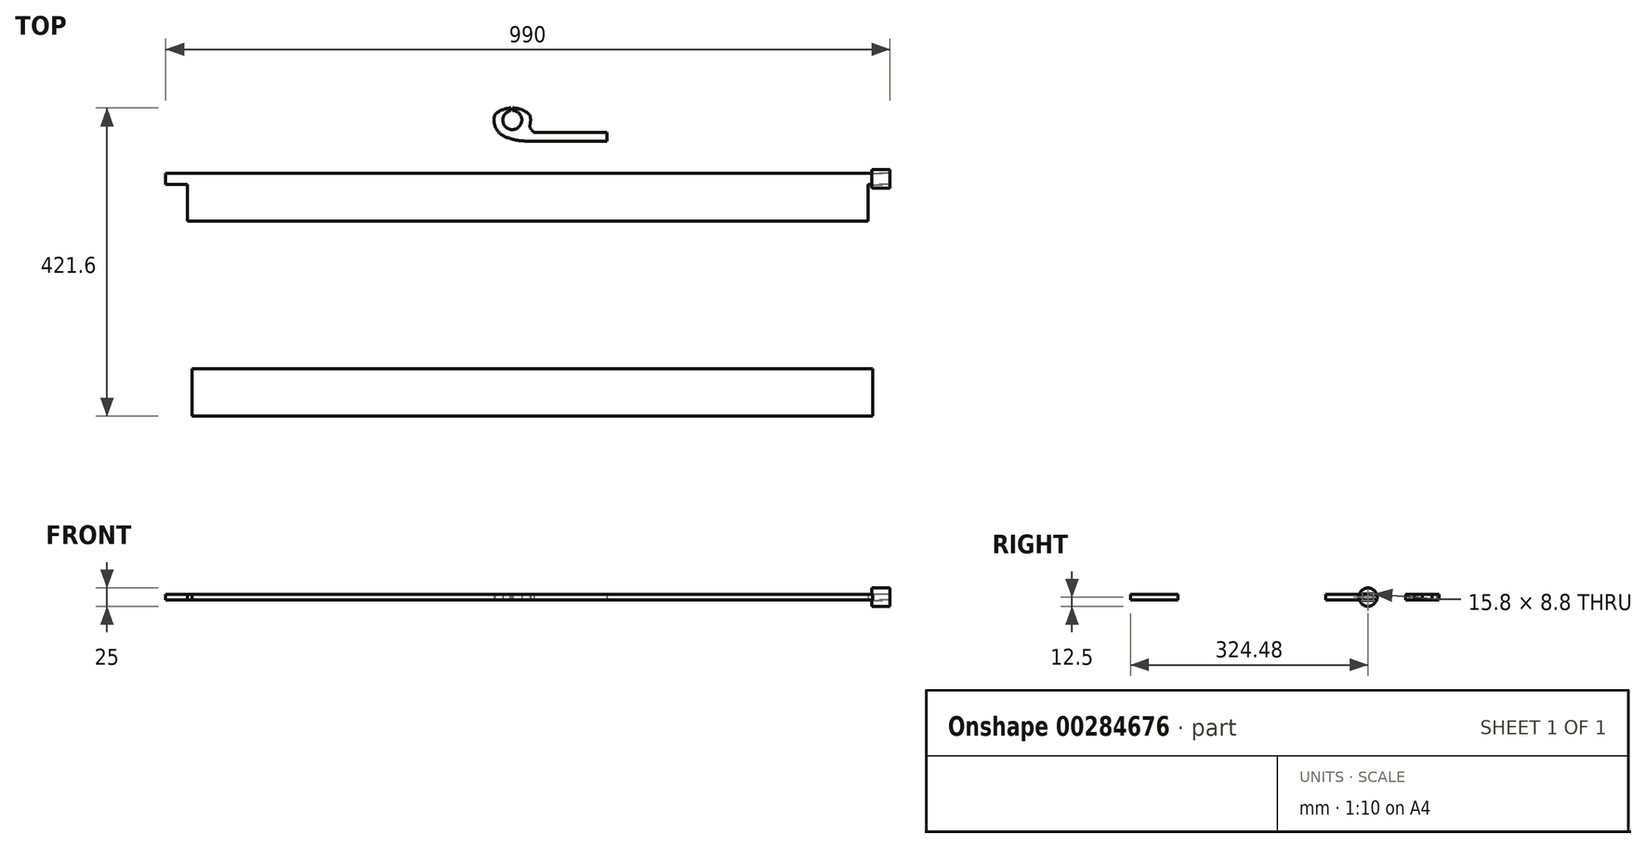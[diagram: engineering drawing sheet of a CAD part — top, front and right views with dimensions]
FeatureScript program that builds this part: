
annotation { "Feature Type Name" : "Feature", "Feature Type Description" : "" }
export const myFeature = defineFeature(function(context is Context, id is Id, definition is map)
    precondition{}
    {
        {
            var Q0;
            Q0=qCreatedBy(makeId("Top.planeOp"),FACE);
            var sketch = newSketch(context, id + "F0", { "sketchPlane" : qUnion([Q0])});
            skLineSegment(sketch, "E0.bottom", {"start": v(495, 7.5) * mm, "end": v(-495, 7.5) * mm});
            skLineSegment(sketch, "E0.top", {"start": v(495, -7.5) * mm, "end": v(465, -7.5) * mm});
            skLineSegment(sketch, "E0.left", {"start": v(495, 7.5) * mm, "end": v(495, -7.5) * mm});
            skLineSegment(sketch, "E0.right", {"start": v(-495, 7.5) * mm, "end": v(-495, -7.5) * mm});
            skPoint(sketch, "E0.middle", {"position": v(0, 0) * mm});
            skLineSegment(sketch, "E1", {"start": v(495, 0) * mm, "end": v(465, 0) * mm, "construction": true});
            skLineSegment(sketch, "E2.top", {"start": v(465, -57.5) * mm, "end": v(-465, -57.5) * mm});
            skLineSegment(sketch, "E2.left", {"start": v(465, -7.5) * mm, "end": v(465, -57.5) * mm});
            skLineSegment(sketch, "E2.right", {"start": v(-465, -7.5) * mm, "end": v(-465, -57.5) * mm});
            skLineSegment(sketch, "E3", {"start": v(-495, 0) * mm, "end": v(-465, 0) * mm, "construction": true});
            skLineSegment(sketch, "E4.trimOffspring", {"start": v(-465, -7.5) * mm, "end": v(-495, -7.5) * mm});
            skLineSegment(sketch, "E5.bottom", {"start": v(-465, -57.5) * mm, "end": v(-465, -57.5) * mm});
            skLineSegment(sketch, "E5.top", {"start": v(-465, 7.5) * mm, "end": v(-465, 7.5) * mm});
            skLineSegment(sketch, "E5.left", {"start": v(-465, -57.5) * mm, "end": v(-465, 7.5) * mm});
            skLineSegment(sketch, "E5.right", {"start": v(-465, -57.5) * mm, "end": v(-465, 7.5) * mm});
            skLineSegment(sketch, "E6.top", {"start": v(465, 7.5) * mm, "end": v(-465, 7.5) * mm});
            skLineSegment(sketch, "E6.left", {"start": v(465, -57.5) * mm, "end": v(465, 7.5) * mm});
            skLineSegment(sketch, "E7.bottom", {"start": v(-458.64, -324.48) * mm, "end": v(471.36, -324.48) * mm});
            skLineSegment(sketch, "E7.top", {"start": v(-458.64, -259.48) * mm, "end": v(471.36, -259.48) * mm});
            skLineSegment(sketch, "E7.left", {"start": v(-458.64, -324.48) * mm, "end": v(-458.64, -259.48) * mm});
            skLineSegment(sketch, "E7.right", {"start": v(471.36, -324.48) * mm, "end": v(471.36, -259.48) * mm});
            skSolve(sketch);
        }
        {
            var Q0;
            Q0=qSketchRegion(id+"F0",true);
            extrude(context, id + "F1", {"entities" : qUnion([Q0]), "depth" : 8 * mm});
        }
        {
            var Q0;
            Q0=makeQuery(id+"F1.opExtrude","SWEPT_FACE",FACE,{"disambiguationData":[OSD([sQuery(id+"F0.wireOp",EDGE,"E0.left")])]});
            var sketch = newSketch(context, id + "F2", { "sketchPlane" : qUnion([Q0])});
            skLineSegment(sketch, "E8.0.0", {"start": v(-7.5, 0) * mm, "end": v(7.5, 0) * mm});
            skLineSegment(sketch, "E8.0.1", {"start": v(7.5, 0) * mm, "end": v(7.5, 8) * mm});
            skLineSegment(sketch, "E8.0.2", {"start": v(7.5, 8) * mm, "end": v(-7.5, 8) * mm});
            skLineSegment(sketch, "E8.0.3", {"start": v(-7.5, 8) * mm, "end": v(-7.5, 0) * mm});
            skLineSegment(sketch, "E9", {"start": v(0, 8) * mm, "end": v(0, 0) * mm, "construction": true});
            skLineSegment(sketch, "E10", {"start": v(7.5, 4) * mm, "end": v(-7.5, 4) * mm, "construction": true});
            skLineSegment(sketch, "E11.0", {"start": v(-7.9, -0.4) * mm, "end": v(7.9, -0.4) * mm});
            skLineSegment(sketch, "E11.1", {"start": v(-7.9, 8.4) * mm, "end": v(-7.9, -0.4) * mm});
            skLineSegment(sketch, "E11.2", {"start": v(7.9, 8.4) * mm, "end": v(-7.9, 8.4) * mm});
            skLineSegment(sketch, "E11.3", {"start": v(7.9, -0.4) * mm, "end": v(7.9, 8.4) * mm});
            skCircle(sketch, "E12", {"center": v(0, 4) * mm, "radius": 12.5 * mm});
            skSolve(sketch);
        }
        {
            var Q0;
            Q0=qSketchRegion(id+"F2",true);
            extrude(context, id + "F3", {"entities" : qUnion([Q0]), "oppositeDirection" : true, "depth" : 25 * mm});
        }
        {
            var Q0;
            Q0=qCreatedBy(makeId("Top.planeOp"),FACE);
            var sketch = newSketch(context, id + "F4", { "sketchPlane" : qUnion([Q0])});
            skLineSegment(sketch, "E13.bottom", {"start": v(108.34, 63.38) * mm, "end": v(8.34, 63.38) * mm});
            skLineSegment(sketch, "E13.top", {"start": v(108.34, 51.38) * mm, "end": v(8.34, 51.38) * mm});
            skLineSegment(sketch, "E13.left", {"start": v(108.34, 63.38) * mm, "end": v(108.34, 51.38) * mm});
            skArc(sketch, "E14", {"start": v(2.5, 72.7) * mm, "mid": v(3.77, 80.08) * mm, "end": v(2.79, 87.52) * mm});
            skFitSpline(sketch, "E15", {"points": [v(8.34, 51.38) * mm, v(-24.8, 55.83) * mm, v(-32.24, 64.09) * mm], "startDerivative": vector(-64.88, 1.85) * mm, "endDerivative": vector(-14.53, 25.37) * mm});
            skFitSpline(sketch, "E16", {"points": [v(8.34, 63.38) * mm, v(2.5, 72.7) * mm, v(6.49, 78.19) * mm], "startDerivative": vector(-15.95, 17.8) * mm, "endDerivative": vector(13.4, 11.56) * mm});
            skArc(sketch, "E17", {"start": v(-23.03, 93.44) * mm, "mid": v(-20.5, 67.59) * mm, "end": v(-20.86, 93.56) * mm});
            skLineSegment(sketch, "E18", {"start": v(-23.03, 93.44) * mm, "end": v(-23.03, 97.08) * mm});
            skLineSegment(sketch, "E19", {"start": v(-20.86, 93.56) * mm, "end": v(-20.86, 97.12) * mm});
            skArc(sketch, "E20.trimOffspring", {"start": v(-45.13, 87.88) * mm, "mid": v(-42.34, 67.18) * mm, "end": v(-24.8, 55.83) * mm});
            skArc(sketch, "E21", {"start": v(2.79, 87.52) * mm, "mid": v(-8.14, 94.54) * mm, "end": v(-20.86, 97.12) * mm});
            skArc(sketch, "E22.trimOffspring", {"start": v(-23.03, 97.08) * mm, "mid": v(-34.89, 94.42) * mm, "end": v(-45.13, 87.88) * mm});
            skSolve(sketch);
        }
        {
            var Q0;
            Q0=makeQuery(id+"F4.imprint","IMPRINT",FACE,{"disambiguationData":[TD([[makeQuery(id+"F4.imprint","IMPRINT",EDGE,{"derivedFrom":sQuery(id+"F4.wireOp",EDGE,"E13.bottom")}),1.0]])]});
            extrude(context, id + "F5", {"entities" : qUnion([Q0]), "depth" : 8 * mm});
        }
    });
